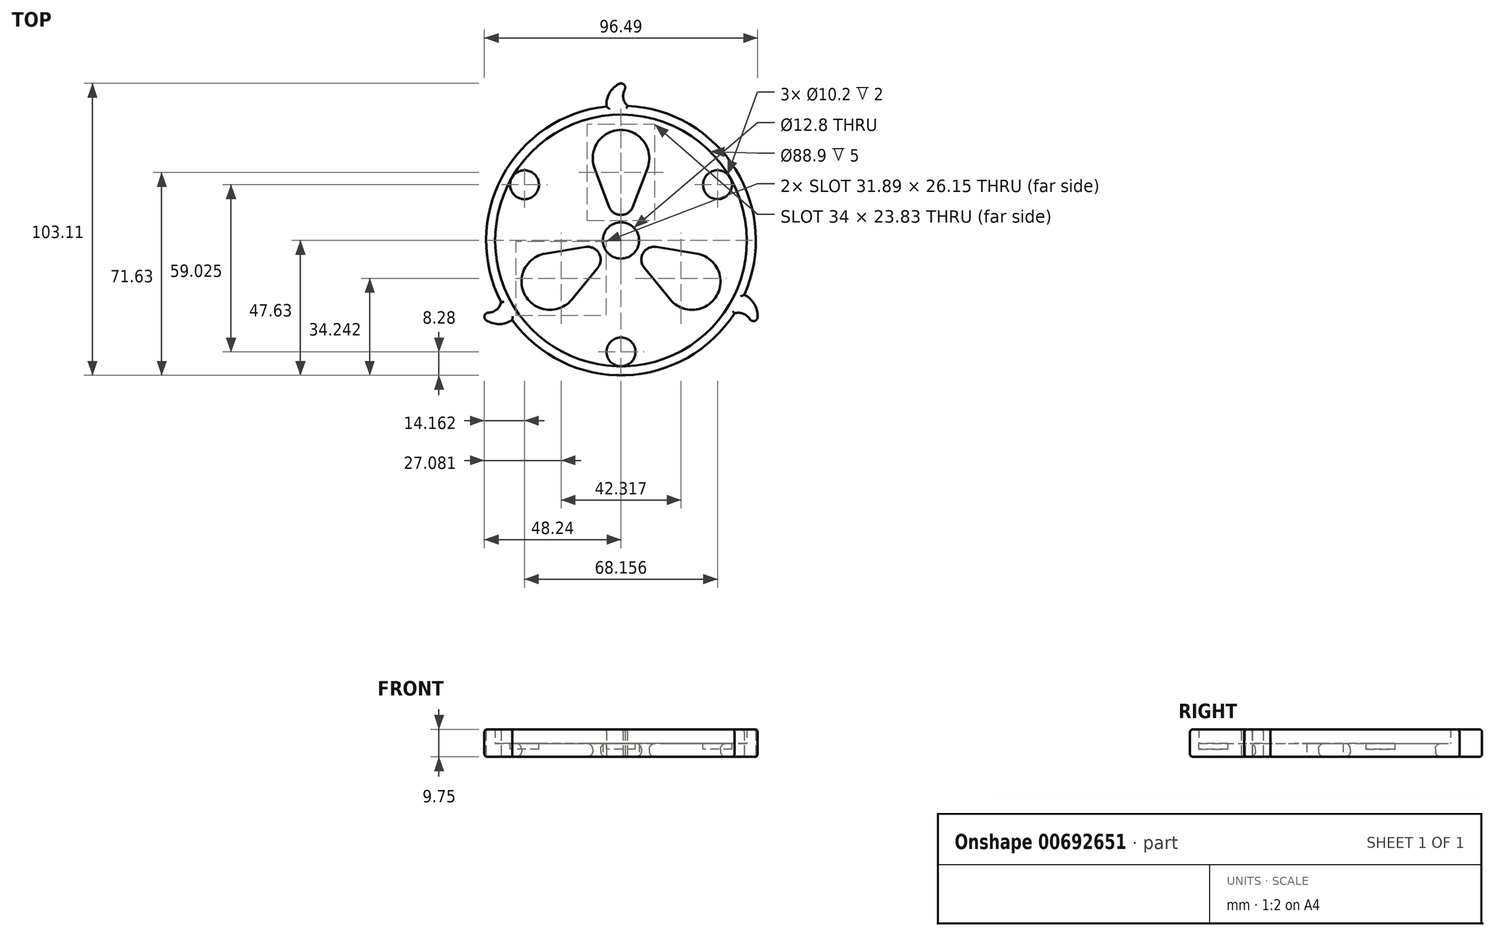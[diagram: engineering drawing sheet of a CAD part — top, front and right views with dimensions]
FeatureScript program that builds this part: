
annotation { "Feature Type Name" : "Feature", "Feature Type Description" : "" }
export const myFeature = defineFeature(function(context is Context, id is Id, definition is map)
    precondition{}
    {
        {
            var Q0;
            Q0=qCreatedBy(makeId("Top.planeOp"),FACE);
            var sketch = newSketch(context, id + "F0", { "sketchPlane" : qUnion([Q0])});
            skArc(sketch, "E0", {"start": v(-5.16, 47.34) * mm, "mid": v(-41.95, 22.55) * mm, "end": v(-42.34, -21.81) * mm});
            skCircle(sketch, "E1", {"center": v(0, 0) * mm, "radius": 44.45 * mm});
            skCircle(sketch, "E2", {"center": v(0, 0) * mm, "radius": 6.4 * mm});
            skArc(sketch, "E3", {"start": v(-4.2, 11.9) * mm, "mid": v(0, 9) * mm, "end": v(4.2, 11.9) * mm});
            skArc(sketch, "E4", {"start": v(9.35, 25.45) * mm, "mid": v(0, 39) * mm, "end": v(-9.35, 25.45) * mm});
            skLineSegment(sketch, "E5", {"start": v(-9.35, 25.45) * mm, "end": v(-4.2, 11.9) * mm});
            skLineSegment(sketch, "E6", {"start": v(9.35, 25.45) * mm, "end": v(4.2, 11.9) * mm});
            skArc(sketch, "E7.1.0", {"start": v(-26.72, -4.63) * mm, "mid": v(-33.77, -19.5) * mm, "end": v(-17.37, -20.82) * mm});
            skLineSegment(sketch, "E7.1.1", {"start": v(-17.37, -20.82) * mm, "end": v(-8.2, -9.6) * mm});
            skLineSegment(sketch, "E7.1.2", {"start": v(-26.72, -4.63) * mm, "end": v(-12.41, -2.3) * mm});
            skArc(sketch, "E7.1.3", {"start": v(-8.2, -9.6) * mm, "mid": v(-7.8, -4.5) * mm, "end": v(-12.41, -2.3) * mm});
            skArc(sketch, "E7.2.0", {"start": v(17.37, -20.82) * mm, "mid": v(33.77, -19.5) * mm, "end": v(26.72, -4.63) * mm});
            skLineSegment(sketch, "E7.2.1", {"start": v(26.72, -4.63) * mm, "end": v(12.41, -2.3) * mm});
            skLineSegment(sketch, "E7.2.2", {"start": v(17.37, -20.82) * mm, "end": v(8.2, -9.6) * mm});
            skArc(sketch, "E7.2.3", {"start": v(12.41, -2.3) * mm, "mid": v(7.8, -4.5) * mm, "end": v(8.2, -9.6) * mm});
            skPoint(sketch, "E8", {"position": v(0, 53.98) * mm});
            skArc(sketch, "E9", {"start": v(1.32, 53.26) * mm, "mid": v(1.06, 55.04) * mm, "end": v(-0.72, 55.3) * mm});
            skLineSegment(sketch, "E10", {"start": v(-0.72, 55.3) * mm, "end": v(3.1, 57.36) * mm, "construction": true});
            skArc(sketch, "E11", {"start": v(-0.72, 55.3) * mm, "mid": v(-4.09, 51.96) * mm, "end": v(-5.16, 47.34) * mm});
            skLineSegment(sketch, "E12", {"start": v(1.32, 53.26) * mm, "end": v(3.2, 56.72) * mm, "construction": true});
            skArc(sketch, "E13", {"start": v(1.32, 53.26) * mm, "mid": v(0.82, 50.25) * mm, "end": v(2.28, 47.57) * mm});
            skArc(sketch, "E14.1.0", {"start": v(-47.53, -28.27) * mm, "mid": v(-42.96, -29.52) * mm, "end": v(-38.42, -28.14) * mm});
            skArc(sketch, "E14.1.1", {"start": v(-46.79, -25.49) * mm, "mid": v(-43.93, -24.42) * mm, "end": v(-42.34, -21.81) * mm});
            skArc(sketch, "E14.1.2", {"start": v(-46.79, -25.49) * mm, "mid": v(-48.2, -26.6) * mm, "end": v(-47.53, -28.27) * mm});
            skArc(sketch, "E14.2.0", {"start": v(48.24, -27.03) * mm, "mid": v(47.05, -22.44) * mm, "end": v(43.58, -19.2) * mm});
            skArc(sketch, "E14.2.1", {"start": v(45.47, -27.77) * mm, "mid": v(43.1, -25.84) * mm, "end": v(40.06, -25.76) * mm});
            skArc(sketch, "E14.2.2", {"start": v(45.47, -27.77) * mm, "mid": v(47.13, -28.44) * mm, "end": v(48.24, -27.03) * mm});
            skArc(sketch, "E15.trimOffspring", {"start": v(43.58, -19.2) * mm, "mid": v(40.5, 25.05) * mm, "end": v(2.28, 47.57) * mm});
            skArc(sketch, "E16.trimOffspring", {"start": v(-38.42, -28.14) * mm, "mid": v(1.44, -47.6) * mm, "end": v(40.06, -25.76) * mm});
            skLineSegment(sketch, "E17", {"start": v(0, 0) * mm, "end": v(-27.82, 27.82) * mm, "construction": true});
            skSolve(sketch);
        }
        {
            var Q0;
            Q0=makeQuery(id+"F0.imprint","IMPRINT",FACE,{"disambiguationData":[TD([[makeQuery(id+"F0.imprint","IMPRINT",EDGE,{"derivedFrom":sQuery(id+"F0.wireOp",EDGE,"E2")}),-1.0]])]});
            extrude(context, id + "F1", {"entities" : qUnion([Q0]), "depth" : 4.75 * mm, "offsetDistance" : 25 * mm});
        }
        {
            var Q0;
            Q0=makeQuery(id+"F0.imprint","IMPRINT",FACE,{"disambiguationData":[TD([[makeQuery(id+"F0.imprint","IMPRINT",EDGE,{"derivedFrom":sQuery(id+"F0.wireOp",EDGE,"E0")}),1.0]])]});
            extrude(context, id + "F2", {"entities" : qUnion([Q0]), "operationType" : NewBodyOperationType.ADD, "depth" : 4.75 * mm + 5 * mm, "offsetDistance" : 25 * mm});
        }
        {
            var Q0;
            Q0=makeQuery(id+"F2.opExtrude","CAP_EDGE",EDGE,{"disambiguationData":[OSD([sQuery(id+"F0.wireOp",EDGE,"E0")])],"isStart":false});
            var Q1;
            Q1=makeQuery(id+"F2.opExtrude","CAP_EDGE",EDGE,{"disambiguationData":[OSD([sQuery(id+"F0.wireOp",EDGE,"E14.1.1")])],"isStart":false});
            var Q2;
            Q2=makeQuery(id+"F2.opExtrude","CAP_EDGE",EDGE,{"disambiguationData":[OSD([sQuery(id+"F0.wireOp",EDGE,"E16.trimOffspring")])],"isStart":false});
            var Q3;
            Q3=makeQuery(id+"F2.opExtrude","CAP_EDGE",EDGE,{"disambiguationData":[OSD([sQuery(id+"F0.wireOp",EDGE,"E14.1.0")])],"isStart":false});
            var Q4;
            Q4=makeQuery(id+"F2.opExtrude","CAP_EDGE",EDGE,{"disambiguationData":[OSD([sQuery(id+"F0.wireOp",EDGE,"E14.1.2")])],"isStart":false});
            var Q5;
            Q5=makeQuery(id+"F2.opExtrude","CAP_EDGE",EDGE,{"disambiguationData":[OSD([sQuery(id+"F0.wireOp",EDGE,"E14.2.1")])],"isStart":false});
            var Q6;
            Q6=makeQuery(id+"F2.opExtrude","CAP_EDGE",EDGE,{"disambiguationData":[OSD([sQuery(id+"F0.wireOp",EDGE,"E15.trimOffspring")])],"isStart":false});
            var Q7;
            Q7=makeQuery(id+"F2.opExtrude","CAP_EDGE",EDGE,{"disambiguationData":[OSD([sQuery(id+"F0.wireOp",EDGE,"E13")])],"isStart":false});
            var Q8;
            Q8=makeQuery(id+"F2.opExtrude","CAP_EDGE",EDGE,{"disambiguationData":[OSD([sQuery(id+"F0.wireOp",EDGE,"E0")])],"isStart":true});
            var Q9;
            Q9=makeQuery(id+"F2.opExtrude","CAP_EDGE",EDGE,{"disambiguationData":[OSD([sQuery(id+"F0.wireOp",EDGE,"E14.1.1")])],"isStart":true});
            var Q10;
            Q10=makeQuery(id+"F2.opExtrude","CAP_EDGE",EDGE,{"disambiguationData":[OSD([sQuery(id+"F0.wireOp",EDGE,"E16.trimOffspring")])],"isStart":true});
            var Q11;
            Q11=makeQuery(id+"F2.opExtrude","CAP_EDGE",EDGE,{"disambiguationData":[OSD([sQuery(id+"F0.wireOp",EDGE,"E14.2.1")])],"isStart":true});
            var Q12;
            Q12=makeQuery(id+"F2.opExtrude","CAP_EDGE",EDGE,{"disambiguationData":[OSD([sQuery(id+"F0.wireOp",EDGE,"E15.trimOffspring")])],"isStart":true});
            var Q13;
            Q13=makeQuery(id+"F2.opExtrude","CAP_EDGE",EDGE,{"disambiguationData":[OSD([sQuery(id+"F0.wireOp",EDGE,"E13")])],"isStart":true});
            fillet(context, id + "F3", {"entities" : qUnion([Q0, Q1, Q2, Q3, Q4, Q5, Q6, Q7, Q8, Q9, Q10, Q11, Q12, Q13]), "radius" : 1 * mm, "tangentPropagation" : true, "allowEdgeOverflow" : false});
        }
        {
            var Q0;
            Q0=makeQuery(id+"F1.opExtrude","CAP_FACE",FACE,{"disambiguationData":[OSD([sQuery(id+"F0.wireOp",EDGE,"E1"),sQuery(id+"F0.wireOp",EDGE,"E2"),sQuery(id+"F0.wireOp",EDGE,"E3"),sQuery(id+"F0.wireOp",EDGE,"E4"),sQuery(id+"F0.wireOp",EDGE,"E5"),sQuery(id+"F0.wireOp",EDGE,"E6"),sQuery(id+"F0.wireOp",EDGE,"E7.1.0"),sQuery(id+"F0.wireOp",EDGE,"E7.1.1"),sQuery(id+"F0.wireOp",EDGE,"E7.1.2"),sQuery(id+"F0.wireOp",EDGE,"E7.1.3"),sQuery(id+"F0.wireOp",EDGE,"E7.2.0"),sQuery(id+"F0.wireOp",EDGE,"E7.2.1"),sQuery(id+"F0.wireOp",EDGE,"E7.2.2"),sQuery(id+"F0.wireOp",EDGE,"E7.2.3")])],"isStart":false});
            var sketch = newSketch(context, id + "F4", { "sketchPlane" : qUnion([Q0])});
            skLineSegment(sketch, "E18", {"start": v(-11.7, -6.75) * mm, "end": v(34.08, 19.67) * mm, "construction": true});
            skCircle(sketch, "E19", {"center": v(34.08, 19.67) * mm, "radius": 5.1 * mm});
            skCircle(sketch, "E20.1.0", {"center": v(-34.08, 19.68) * mm, "radius": 5.1 * mm});
            skCircle(sketch, "E20.2.0", {"center": v(0, -39.35) * mm, "radius": 5.1 * mm});
            skPoint(sketch, "E20.center", {"position": v(0, 0) * mm});
            skSolve(sketch);
        }
        {
            var Q0;
            Q0 = qSketchRegion(id + "F4", true);
            extrude(context, id + "F5", {"entities" : qUnion([Q0]), "operationType" : NewBodyOperationType.REMOVE, "oppositeDirection" : true, "depth" : 2 * mm, "offsetDistance" : 25 * mm});
        }
        {
            var Q0;
            Q0=makeQuery(id+"F1.opExtrude","CAP_EDGE",EDGE,{"disambiguationData":[OSD([sQuery(id+"F0.wireOp",EDGE,"E7.1.2")])],"isStart":false});
            var Q1;
            Q1=makeQuery(id+"F1.opExtrude","CAP_EDGE",EDGE,{"disambiguationData":[OSD([sQuery(id+"F0.wireOp",EDGE,"E7.1.2")])],"isStart":true});
            var Q2;
            Q2=makeQuery(id+"F1.opExtrude","CAP_EDGE",EDGE,{"disambiguationData":[OSD([sQuery(id+"F0.wireOp",EDGE,"E5")])],"isStart":false});
            var Q3;
            Q3=makeQuery(id+"F1.opExtrude","CAP_EDGE",EDGE,{"disambiguationData":[OSD([sQuery(id+"F0.wireOp",EDGE,"E5")])],"isStart":true});
            var Q4;
            Q4=makeQuery(id+"F1.opExtrude","CAP_EDGE",EDGE,{"disambiguationData":[OSD([sQuery(id+"F0.wireOp",EDGE,"E7.2.3")])],"isStart":true});
            var Q5;
            Q5=makeQuery(id+"F1.opExtrude","CAP_EDGE",EDGE,{"disambiguationData":[OSD([sQuery(id+"F0.wireOp",EDGE,"E7.2.1")])],"isStart":false});
            fillet(context, id + "F6", {"entities" : qUnion([Q0, Q1, Q2, Q3, Q4, Q5]), "radius" : 2 * mm, "tangentPropagation" : true, "allowEdgeOverflow" : false});
        }
    });
